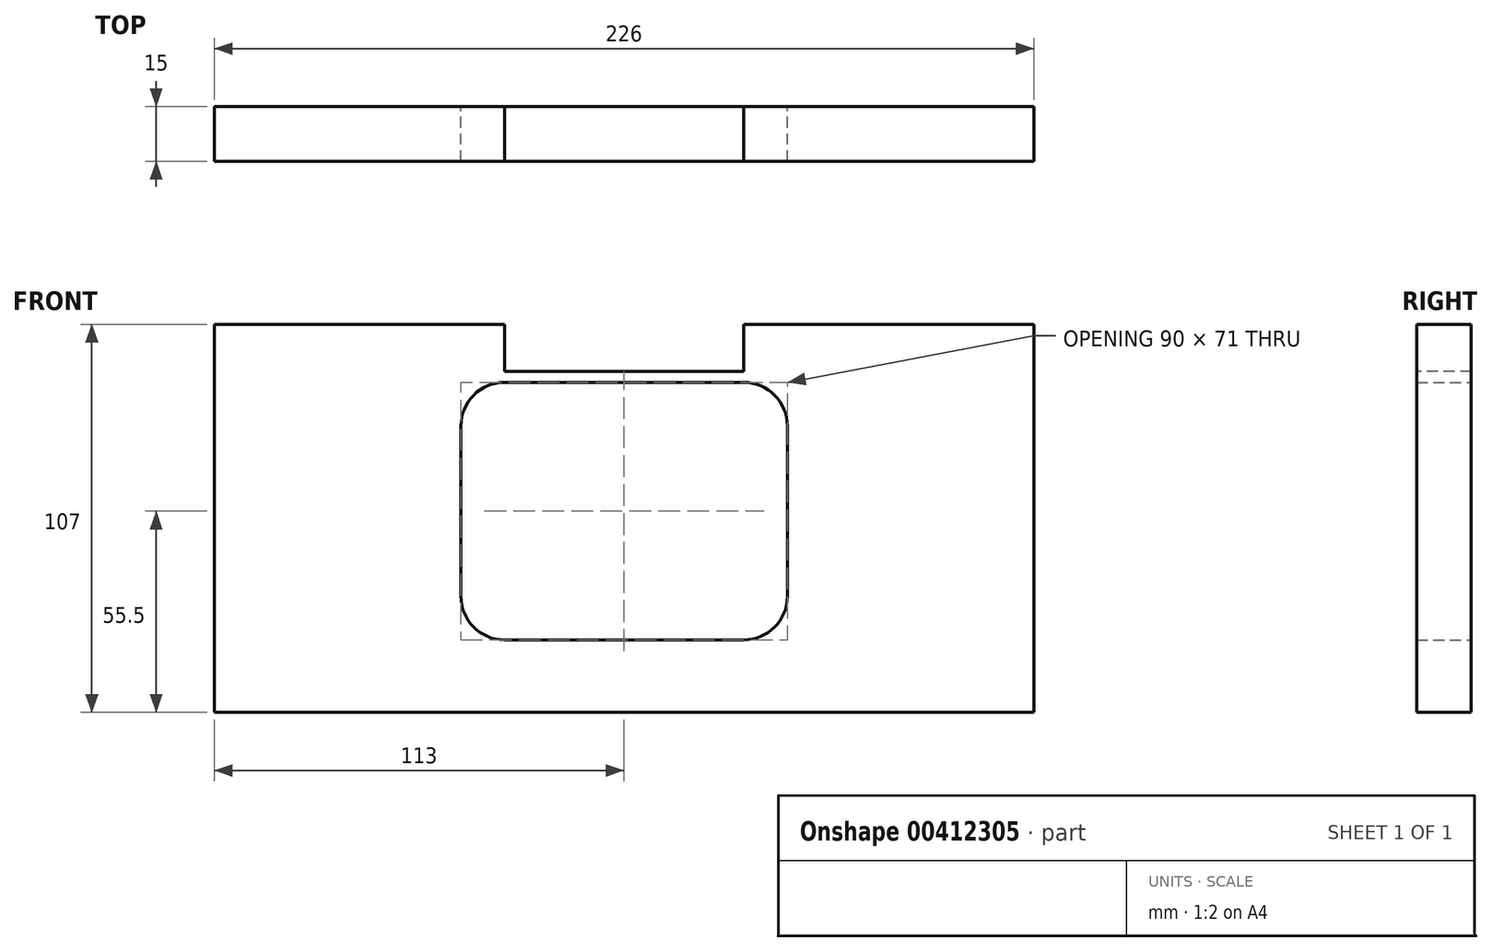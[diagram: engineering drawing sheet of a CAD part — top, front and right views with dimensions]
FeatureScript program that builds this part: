
annotation { "Feature Type Name" : "Feature", "Feature Type Description" : "" }
export const myFeature = defineFeature(function(context is Context, id is Id, definition is map)
    precondition{}
    {
        {
            var Q0;
            Q0=qCreatedBy(makeId("Front.planeOp"),FACE);
            var sketch = newSketch(context, id + "F0", { "sketchPlane" : qUnion([Q0])});
            skLineSegment(sketch, "E0.bottom", {"start": v(113, 55.5) * mm, "end": v(-113, 55.5) * mm});
            skLineSegment(sketch, "E0.top", {"start": v(113, -55.5) * mm, "end": v(-113, -55.5) * mm});
            skLineSegment(sketch, "E0.left", {"start": v(113, 55.5) * mm, "end": v(113, -55.5) * mm});
            skLineSegment(sketch, "E0.right", {"start": v(-113, 55.5) * mm, "end": v(-113, -55.5) * mm});
            skPoint(sketch, "E0.middle", {"position": v(0, 0) * mm});
            skLineSegment(sketch, "E1.bottom", {"start": v(45, 35.5) * mm, "end": v(-45, 35.5) * mm});
            skLineSegment(sketch, "E1.top", {"start": v(45, -35.5) * mm, "end": v(-45, -35.5) * mm});
            skLineSegment(sketch, "E1.left", {"start": v(45, 35.5) * mm, "end": v(45, -35.5) * mm});
            skLineSegment(sketch, "E1.right", {"start": v(-45, 35.5) * mm, "end": v(-45, -35.5) * mm});
            skSolve(sketch);
        }
        {
            var Q0;
            Q0 = qSketchRegion(id + "F0", true);
            extrude(context, id + "F1", {"entities" : qUnion([Q0]), "depth" : 15 * mm});
        }
        {
            var Q0;
            Q0=makeQuery(id+"F1.opExtrude","SWEPT_EDGE",EDGE,{"disambiguationData":[OSD([sQuery(id+"F0.wireOp",EDGE,"E1.bottom"),sQuery(id+"F0.wireOp",EDGE,"E1.left")])]});
            var Q1;
            Q1=makeQuery(id+"F1.opExtrude","SWEPT_EDGE",EDGE,{"disambiguationData":[OSD([sQuery(id+"F0.wireOp",EDGE,"E1.top"),sQuery(id+"F0.wireOp",EDGE,"E1.left")])]});
            var Q2;
            Q2=makeQuery(id+"F1.opExtrude","SWEPT_EDGE",EDGE,{"disambiguationData":[OSD([sQuery(id+"F0.wireOp",EDGE,"E1.top"),sQuery(id+"F0.wireOp",EDGE,"E1.right")])]});
            var Q3;
            Q3=makeQuery(id+"F1.opExtrude","SWEPT_EDGE",EDGE,{"disambiguationData":[OSD([sQuery(id+"F0.wireOp",EDGE,"E1.bottom"),sQuery(id+"F0.wireOp",EDGE,"E1.right")])]});
            fillet(context, id + "F2", {"entities" : qUnion([Q0, Q1, Q2, Q3]), "radius" : 12 * mm, "tangentPropagation" : true, "allowEdgeOverflow" : false});
        }
        {
            var Q0;
            Q0=makeQuery(id+"F1.opExtrude","CAP_FACE",FACE,{"disambiguationData":[OSD([sQuery(id+"F0.wireOp",EDGE,"E0.bottom"),sQuery(id+"F0.wireOp",EDGE,"E0.top"),sQuery(id+"F0.wireOp",EDGE,"E0.left"),sQuery(id+"F0.wireOp",EDGE,"E0.right"),sQuery(id+"F0.wireOp",EDGE,"E1.bottom"),sQuery(id+"F0.wireOp",EDGE,"E1.top"),sQuery(id+"F0.wireOp",EDGE,"E1.left"),sQuery(id+"F0.wireOp",EDGE,"E1.right")])],"isStart":false});
            var sketch = newSketch(context, id + "F3", { "sketchPlane" : qUnion([Q0])});
            skLineSegment(sketch, "E2", {"start": v(33, 35.5) * mm, "end": v(33, 47.5) * mm, "construction": true});
            skLineSegment(sketch, "E3", {"start": v(-33, 35.5) * mm, "end": v(-33, 47.5) * mm, "construction": true});
            skLineSegment(sketch, "E4", {"start": v(-33, 47.5) * mm, "end": v(-33, 51.5) * mm});
            skLineSegment(sketch, "E5", {"start": v(-33, 51.5) * mm, "end": v(-113, 51.5) * mm});
            skLineSegment(sketch, "E6", {"start": v(-113, 51.5) * mm, "end": v(-113, 55.5) * mm});
            skLineSegment(sketch, "E7", {"start": v(-113, 55.5) * mm, "end": v(113, 55.5) * mm});
            skLineSegment(sketch, "E8", {"start": v(33, 47.5) * mm, "end": v(33, 51.5) * mm});
            skLineSegment(sketch, "E9", {"start": v(33, 51.5) * mm, "end": v(113, 51.5) * mm});
            skLineSegment(sketch, "E10", {"start": v(113, 51.5) * mm, "end": v(113, 55.5) * mm});
            skLineSegment(sketch, "E11", {"start": v(-33, 47.5) * mm, "end": v(-33, 38.5) * mm});
            skLineSegment(sketch, "E12", {"start": v(-33, 38.5) * mm, "end": v(33, 38.5) * mm});
            skLineSegment(sketch, "E13", {"start": v(33, 38.5) * mm, "end": v(33, 47.5) * mm});
            skSolve(sketch);
        }
        {
            var Q0;
            Q0 = qSketchRegion(id + "F3", true);
            extrude(context, id + "F4", {"entities" : qUnion([Q0]), "operationType" : NewBodyOperationType.REMOVE, "oppositeDirection" : true, "depth" : 25 * mm});
        }
    });
